# Revit family: Lighting-Exterior_Accent
name_source: partatom
category: Lighting Fixtures
units: mm (PartAtom-declared; Revit-internal decimal feet)

## family parameters
Always vertical = Yes
Classification Number = 23.80.70.14
Cut with Voids When Loaded = No
Light Source = Yes
Maintain Annotation Orientation = No
Part Type = Normal
Room Calculation Point = No
Round Connector Dimension = Use Diameter
Shared = No
Work Plane-Based = No

## types (1)
- ByType
    A = 1' - 2"
    Amperage = 0.5
    Array = 14
    Assembly Code = D5020200
    Bulb Type = Incandescent_Bulb : 60 Watt Incandescent
    Color Filter = 16777215
    Construction Details = http://www.arcat.com
    Default Elevation = 0' - 0"
    Description = Exterior Accent Luminary as Specified in 16520
    Dimming Lamp Color Temperature Shift = <None>
    Expected Lifespan (Years) = 20
    Green Building-LEED = http://www.arcat.com
    Height Lamp = 1' - 2"
    Keynote = 16520
    Lamp = E26/A19
    Light Source Symbol Size = 0' - 6"
    Maintenance Schedule (Months) = 12
    Manufacturer = Generic
    Manufacturer Fax = (203) 929-2444
    Manufacturer Website = http://www.arcat.com
    Model = Exterior Accent Luminary
    Product Data = http://www.arcat.com
    Product Properties = http://www.arcat.com
    Specification = http://www.arcat.com
    Voltage = 120
    Warranty Duration (Years) = 1

## geometry (parser evidence)
native form markers: Sweep x5
no freeform markers — native parametric forms only
